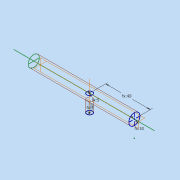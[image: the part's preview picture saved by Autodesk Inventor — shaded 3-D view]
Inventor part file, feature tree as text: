
AUTODESK INVENTOR PART (.ipt)
format: ipt  version: 2019 (Build 230136000, 136)  size: 107,008 bytes
history: native  units: mm
features: other x10, extrude x1, loft x1
ambient origin geometry x8: Origin, YZ Plane, XZ Plane, XY Plane, X Axis, Y Axis, Z Axis, Center Point
bodies: Body1 (feature_tree)
feature tree (12):
  other  "Твердое тело1"
  extrude  "Выдавливание1"  Depth=90.0mm TaperAngle=0.0deg
  other  "цилиндр_конец2"
  other  "РабОсь1"
  other  "РабПлоскость7"
  other  "РабПлоскость8"
  other  "ручка_конец1"
  other  "РабОсь2"
  loft  "Лофт1"
  other  "цилиндр_конец1"
  other  "РабПлоскость9"
  other  "ручка_конец2"
